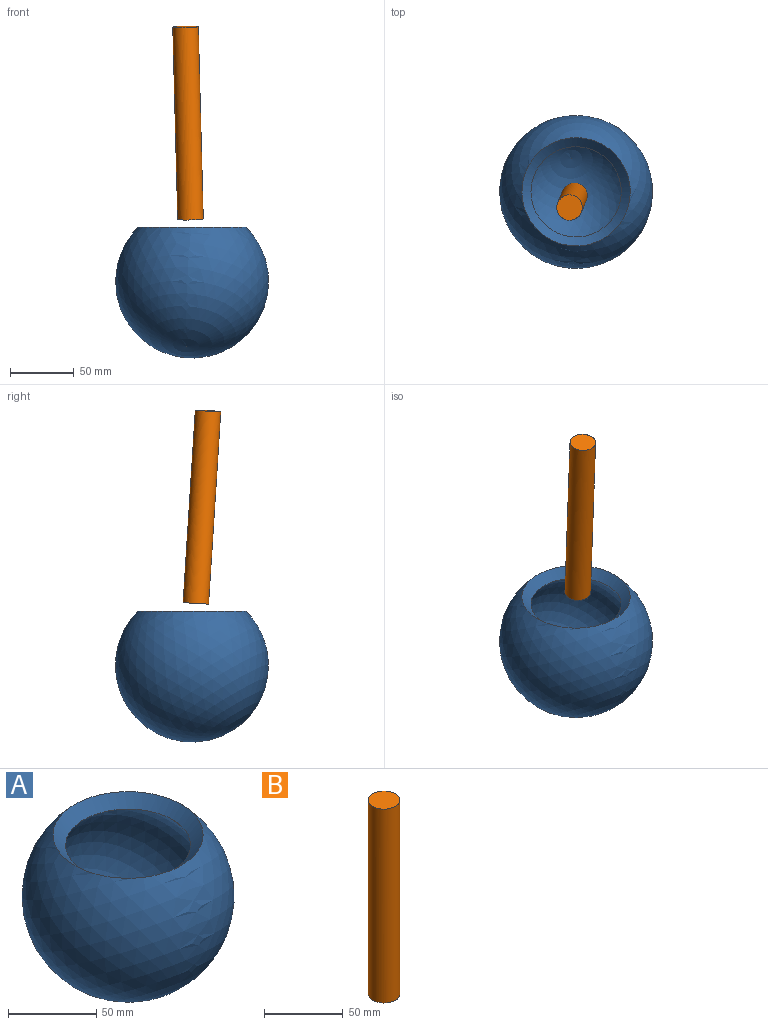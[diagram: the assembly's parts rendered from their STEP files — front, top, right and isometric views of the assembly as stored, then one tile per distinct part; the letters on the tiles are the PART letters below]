
ASSEMBLY  parts=2 mates=1
PART A: 3 faces, bbox 120x120x120 mm
  f0: sphere r=60mm, area 38612.7mm2, adj f1
  f1: cone r=0mm half-angle=45deg, axis (0,0,1), area 2443.6mm2, adj f0,f2
  f2: sphere r=50mm, area 26815.1mm2, adj f1
PART B: 3 faces, bbox 26.2x22.5x152.4 mm
  f0: plane 20.09x20.01mm, normal (0,0,1), area 314.2mm2, adj f1
  f1: cylinder r=10mm len=151.01mm, axis (0,0,1), area 9488.3mm2, adj f0,f2
  f2: sphere r=50mm, area 317.3mm2, adj f1
PLACE A at identity fixed
PLACE B rot(axis=(0.05,0.01,-1),74.8deg) t=(0,0,0)mm
MATE ball B.f1 <-> A.f1  axis (-0.03,-0.06,1) through (0,0,0)mm
